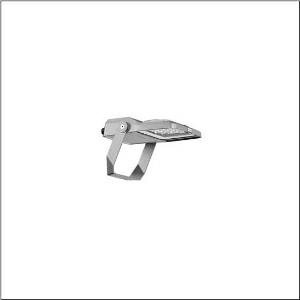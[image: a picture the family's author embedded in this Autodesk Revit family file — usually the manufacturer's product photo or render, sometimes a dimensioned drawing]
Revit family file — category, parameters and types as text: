
# Revit family: floodlight_fl_21_iq_micro___rs12_5xa7761a4b1a_38e5
name_source: partatom
category: Lighting Fixtures
units: mm (PartAtom-declared; Revit-internal decimal feet)

## family parameters
Cut with Voids When Loaded = No
Host = Face
Light Source = No
Part Type = Normal
Room Calculation Point = No
Round Connector Dimension = Use Diameter
Shared = No

## types (1)
- --- (1 x LED, 3220 lm, 23.1 W, 4000K)
    Apparent Load = 23 VA
    CIE Flux Codes = 79 92 99 100 100
    Color Rendering = 70
    Color Temperature = 4000K
    Default Elevation = 1800 mm
    Description = Floodlight FL 21 iQ micro, floodlight, primary light control with lens, of PMMA, primary optical cover: protective disc, of toughened safety glass, transparent, light distribution: RS12, light emission: direct distribution, installation type: surface-mounted, LED, High Power LED, rated luminous flux: 3.220lm, luminous efficacy: 139lm/W, light colour: 740, colour temperature: 4000K, control gear: iQ Comfort/DALI, control: optimised constant luminous flux control (CLO 2.0), Desk-Remote (wireless, voltage-free reading and setting of iQ features in the workshop via application-optimized NFC function/RFID function), Light-Fading, Smart-Wire, Night-Set, Lumen-Switch, Temp-Guard, Auto-Match, with terminal, 6-pole, mains connection: 220..240V, AC, 50/60Hz, start of lifetime: 23W, end of service life: 24W, reduction: 11W, luminaire housing, of diecast aluminium, powder-coated, Siteco® metallic grey (DB 702S), corrosivity category C5 mid according to DIN EN ISO 12944, suitable for swimming pools, chlorine-resistant, sealing non-destructively replaceable, mounting bracket, of steel, galvanised, powder-coated, Siteco® metallic grey (DB 702S), protection rating (complete): IP66, insulation class (complete): insulation class II (safety insulation), certification: CE, ENEC, VDE, protection symbol: D, impact resistance: IK07, permissible operating ambient temperature: -40..+40°C, permissible operating ambient temperature for outdoor applications: -40..+50°C, standard: DIN EN 12944, LABS conformity tested according to VDMA 24364:2018-05, packaging unit: 1 piece

Light Distribution: RS12
    Height = 65 mm
    Lamp = 1 x LED
    Lamp Light Flux = 3220 lm
    Lamp Power = 23.1 W
    Lamp count = 1
    Length = 312 mm
    Luminous efficacy = 139 lm/W
    Manufacturer = Siteco
    ModVariant = No
    Model = 5XA7761A4B1A
    Mounting Place = Wall
    Mounting Type = Surface mounted
    Number of Poles = 1
    OnlyDefault = Yes
    Power Factor = 1
    Product Name = Floodlight FL 21 iQ micro | RS12
    Product group = floodlight | wall mounted
    ProductGroupID = 2001
    Protection Class = Protection class II
    Protection Degree = IP 66
    RLX_Detail_Level = 1
    RLX_Emergency_Light_Flux = 0 lm
    RLX_Emergency_Type = 0
    RLX_Emergency_Type_DB = No
    RlxData = <blob elided: 74969 chars, md5=3c90c338>
    Socket = socket
    Standby Power = 0 W
    System Light Flux = 3220 lm
    System Power = 23 W
    Type Comments = factory setting: luminous flux: 100 % | dim-lin: 254 | 455 mA
    Type Image = l_1006880.jpg
    URL = http://relux.com
    VarID = @adj_181894
    Voltage = 0 V
    Weight = 0.00 kg
    Width = 230 mm

## geometry (parser evidence)
native form markers: Blend x4, Sweep x11
no freeform markers — native parametric forms only
